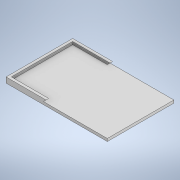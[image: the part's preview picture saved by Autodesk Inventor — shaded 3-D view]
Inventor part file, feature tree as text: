
AUTODESK INVENTOR PART (.ipt)
format: ipt  version: 2022.2 (Build 262287010, 287A)  size: 123,904 bytes
history: native  units: in
note: dims shown in document units (in); Inventor stores cm internally (conversion verified against a paired STEP export)
features: extrude x3, sketch x3, other x1, mirror x1
ambient origin geometry x8: Origin, YZ Plane, XZ Plane, XY Plane, X Axis, Y Axis, Z Axis, Center Point
bodies: Body1 (feature_tree), Body2 (feature_tree), Body3 (feature_tree), Body4 (feature_tree), Body5 (feature_tree)
feature tree (8):
  other  "Sólido1"
  extrude  "Extrusión1"  Depth=1.9685in
  extrude  "Extrusión4"  Depth=0.0787in
  extrude  "Extrusión5"  Depth=0.0787in TaperAngle=0.0deg
  mirror  "Simetría2"
  sketch  "Boceto1"  dims[d0=2.9921in d1=1.9685in]
  sketch  "Boceto2"  dims[d2=0.0787in d3=0.0in d14=0.0787in]
  sketch  "Boceto5"  dims[d15=0.0787in d16=0.0in d19=0.0787in d20=0.0in d4=0.0197in d5=0.0344in d6=0.0197in d7=0.0344in]
